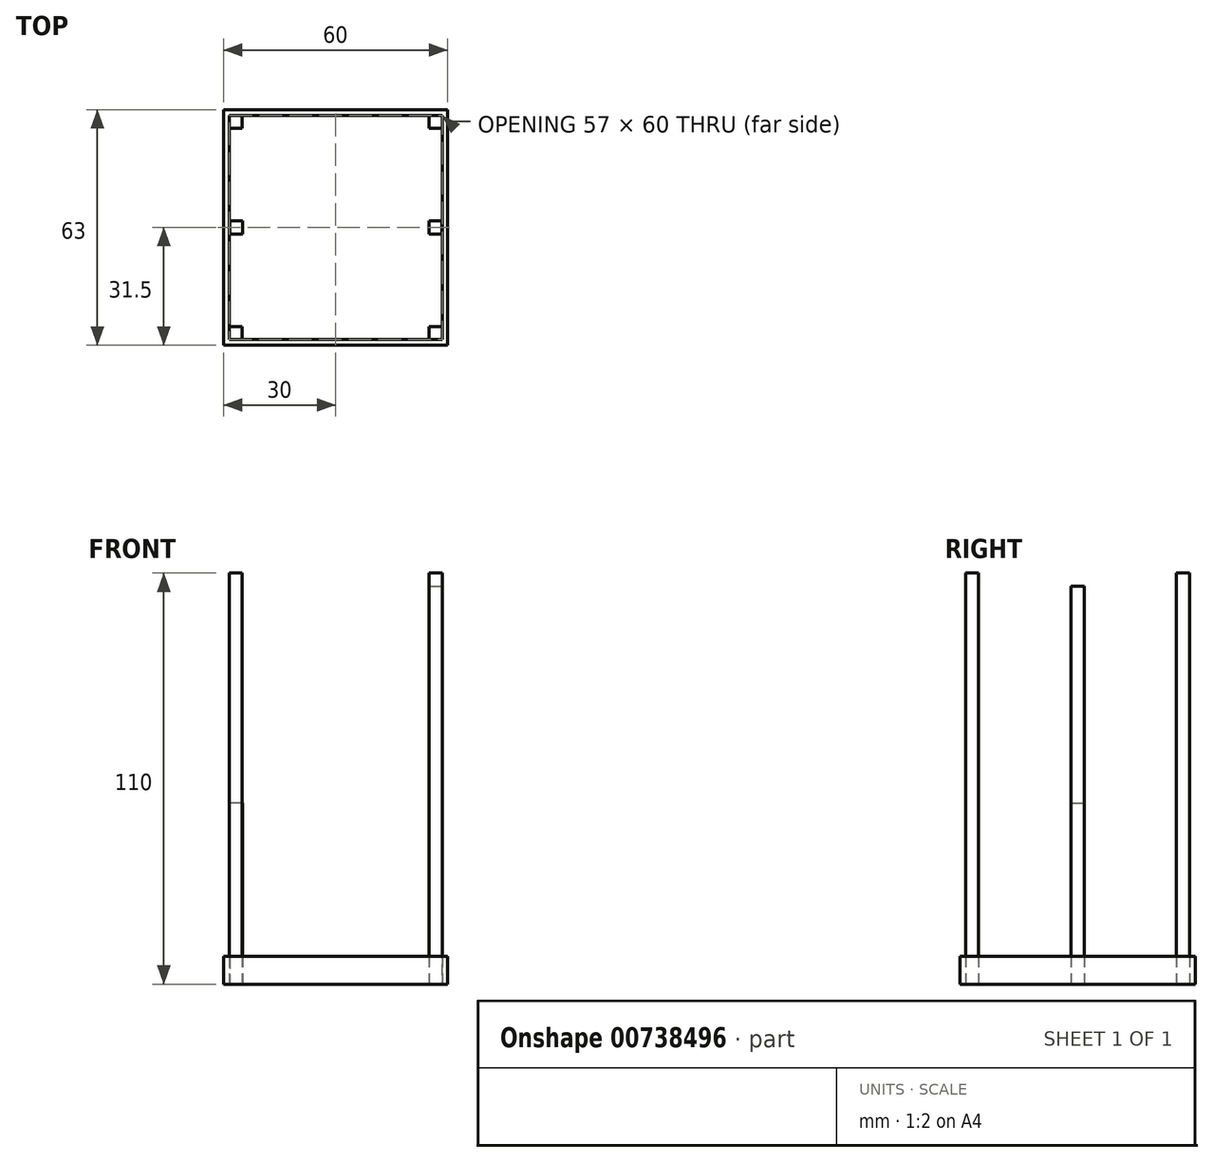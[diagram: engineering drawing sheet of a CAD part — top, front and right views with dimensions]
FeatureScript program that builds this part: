
annotation { "Feature Type Name" : "Feature", "Feature Type Description" : "" }
export const myFeature = defineFeature(function(context is Context, id is Id, definition is map)
    precondition{}
    {
        {
            var Q0;
            Q0=qCreatedBy(makeId("Top.planeOp"),FACE);
            var sketch = newSketch(context, id + "F0", { "sketchPlane" : qUnion([Q0])});
            skLineSegment(sketch, "E0.bottom", {"start": v(30, -31.5) * mm, "end": v(-30, -31.5) * mm});
            skLineSegment(sketch, "E0.top", {"start": v(30, 31.5) * mm, "end": v(-30, 31.5) * mm});
            skLineSegment(sketch, "E0.left", {"start": v(30, -31.5) * mm, "end": v(30, 31.5) * mm});
            skLineSegment(sketch, "E0.right", {"start": v(-30, -31.5) * mm, "end": v(-30, 31.5) * mm});
            skPoint(sketch, "E0.middle", {"position": v(0, 0) * mm});
            skLineSegment(sketch, "E1", {"start": v(30, 30) * mm, "end": v(-30, 30) * mm});
            skLineSegment(sketch, "E2", {"start": v(-28.5, 30) * mm, "end": v(-28.5, -30) * mm});
            skLineSegment(sketch, "E3", {"start": v(28.5, 30) * mm, "end": v(28.5, -30) * mm});
            skLineSegment(sketch, "E4.bottom", {"start": v(-28.5, -30) * mm, "end": v(-25, -30) * mm});
            skLineSegment(sketch, "E4.top", {"start": v(-28.5, -26.5) * mm, "end": v(-25, -26.5) * mm});
            skLineSegment(sketch, "E4.left", {"start": v(-28.5, -30) * mm, "end": v(-28.5, -26.5) * mm});
            skLineSegment(sketch, "E4.right", {"start": v(-25, -30) * mm, "end": v(-25, -26.5) * mm});
            skLineSegment(sketch, "E5.bottom", {"start": v(-28.5, 30) * mm, "end": v(-25, 30) * mm});
            skLineSegment(sketch, "E5.top", {"start": v(-28.5, 26.5) * mm, "end": v(-25, 26.5) * mm});
            skLineSegment(sketch, "E5.left", {"start": v(-28.5, 30) * mm, "end": v(-28.5, 26.5) * mm});
            skLineSegment(sketch, "E5.right", {"start": v(-25, 30) * mm, "end": v(-25, 26.5) * mm});
            skLineSegment(sketch, "E6.bottom", {"start": v(28.5, 30) * mm, "end": v(25, 30) * mm});
            skLineSegment(sketch, "E6.top", {"start": v(28.5, 26.5) * mm, "end": v(25, 26.5) * mm});
            skLineSegment(sketch, "E6.left", {"start": v(28.5, 30) * mm, "end": v(28.5, 26.5) * mm});
            skLineSegment(sketch, "E6.right", {"start": v(25, 30) * mm, "end": v(25, 26.5) * mm});
            skLineSegment(sketch, "E7.bottom", {"start": v(28.5, -30) * mm, "end": v(25, -30) * mm});
            skLineSegment(sketch, "E7.top", {"start": v(28.5, -26.5) * mm, "end": v(25, -26.5) * mm});
            skLineSegment(sketch, "E7.left", {"start": v(28.5, -30) * mm, "end": v(28.5, -26.5) * mm});
            skLineSegment(sketch, "E7.right", {"start": v(25, -30) * mm, "end": v(25, -26.5) * mm});
            skLineSegment(sketch, "E8.bottom", {"start": v(24.95, -1.75) * mm, "end": v(28.45, -1.75) * mm});
            skLineSegment(sketch, "E8.top", {"start": v(24.95, 1.75) * mm, "end": v(28.45, 1.75) * mm});
            skLineSegment(sketch, "E8.left", {"start": v(24.95, -1.75) * mm, "end": v(24.95, 1.75) * mm});
            skLineSegment(sketch, "E8.right", {"start": v(28.45, -1.75) * mm, "end": v(28.45, 1.75) * mm});
            skPoint(sketch, "E8.middle", {"position": v(26.7, 0) * mm});
            skPoint(sketch, "E8.middle.positionSnap0", {"position": v(28.5, 0) * mm});
            skPoint(sketch, "E8.centerSnap0", {"position": v(28.5, 0) * mm});
            skLineSegment(sketch, "E9.bottom", {"start": v(-24.87, -1.75) * mm, "end": v(-28.37, -1.75) * mm});
            skLineSegment(sketch, "E9.top", {"start": v(-24.87, 1.75) * mm, "end": v(-28.37, 1.75) * mm});
            skLineSegment(sketch, "E9.left", {"start": v(-24.87, -1.75) * mm, "end": v(-24.87, 1.75) * mm});
            skLineSegment(sketch, "E9.right", {"start": v(-28.37, -1.75) * mm, "end": v(-28.37, 1.75) * mm});
            skPoint(sketch, "E9.middle", {"position": v(-26.62, 0) * mm});
            skPoint(sketch, "E9.middle.positionSnap0", {"position": v(-28.5, 0) * mm});
            skPoint(sketch, "E9.centerSnap0", {"position": v(-28.5, 0) * mm});
            skLineSegment(sketch, "E10", {"start": v(-30, -30) * mm, "end": v(30, -30) * mm});
            skSolve(sketch);
        }
        {
            var Q0;
            {var subQ3=sQuery(id+"F0.wireOp",EDGE,"E10");var subQ4=sQuery(id+"F0.wireOp",EDGE,"E0.left");var subQ5=makeQuery(id+"F0.imprint","INTERSECT",VERTEX,{"derivedFrom":[subQ4,subQ3]});Q0=makeQuery(id+"F0.imprint","IMPRINT",FACE,{"disambiguationData":[TD([[makeQuery(id+"F0.imprint","IMPRINT",EDGE,{"disambiguationData":[TD([[subQ5,-1.0]])],"derivedFrom":subQ4}),1.0]])]});}
            extrude(context, id + "F1", {"entities" : qUnion([Q0]), "depth" : 7.5 * mm, "offsetDistance" : 25 * mm});
        }
        {
            var Q0;
            {var subQ4=sQuery(id+"F0.wireOp",EDGE,"E0.top");Q0=makeQuery(id+"F0.imprint","IMPRINT",FACE,{"disambiguationData":[TD([[makeQuery(id+"F0.imprint","IMPRINT",EDGE,{"derivedFrom":subQ4}),1.0]])]});}
            extrude(context, id + "F2", {"entities" : qUnion([Q0]), "operationType" : NewBodyOperationType.ADD, "depth" : 7.5 * mm, "offsetDistance" : 25 * mm});
        }
        {
            var Q0;
            {var subQ1=sQuery(id+"F0.wireOp",EDGE,"E0.bottom");Q0=makeQuery(id+"F0.imprint","IMPRINT",FACE,{"disambiguationData":[TD([[makeQuery(id+"F0.imprint","IMPRINT",EDGE,{"derivedFrom":subQ1}),-1.0]])]});}
            var Q1;
            {var subQ0=sQuery(id+"F0.wireOp",EDGE,"E10");var subQ6=sQuery(id+"F0.wireOp",EDGE,"E0.right");var subQ9=makeQuery(id+"F0.imprint","INTERSECT",VERTEX,{"derivedFrom":[subQ6,subQ0]});Q1=makeQuery(id+"F0.imprint","IMPRINT",FACE,{"disambiguationData":[TD([[makeQuery(id+"F0.imprint","IMPRINT",EDGE,{"disambiguationData":[TD([[subQ9,-1.0]])],"derivedFrom":subQ6}),-1.0]])]});}
            extrude(context, id + "F3", {"entities" : qUnion([Q0, Q1]), "operationType" : NewBodyOperationType.ADD, "depth" : 7.5 * mm, "offsetDistance" : 25 * mm});
        }
        {
            var Q0;
            {var subQ4=sQuery(id+"F0.wireOp",EDGE,"E5.top");Q0=makeQuery(id+"F0.imprint","IMPRINT",FACE,{"disambiguationData":[TD([[makeQuery(id+"F0.imprint","IMPRINT",EDGE,{"derivedFrom":subQ4}),1.0]])]});}
            extrude(context, id + "F4", {"entities" : qUnion([Q0]), "operationType" : NewBodyOperationType.ADD, "depth" : 110 * mm, "offsetDistance" : 25 * mm});
        }
        {
            var Q0;
            {var subQ0=sQuery(id+"F0.wireOp",EDGE,"E4.bottom");Q0=makeQuery(id+"F0.imprint","IMPRINT",FACE,{"disambiguationData":[TD([[makeQuery(id+"F0.imprint","IMPRINT",EDGE,{"derivedFrom":subQ0}),1.0]])]});}
            var Q1;
            {var subQ0=sQuery(id+"F0.wireOp",EDGE,"E7.bottom");Q1=makeQuery(id+"F0.imprint","IMPRINT",FACE,{"disambiguationData":[TD([[makeQuery(id+"F0.imprint","IMPRINT",EDGE,{"derivedFrom":subQ0}),-1.0]])]});}
            var Q2;
            {var subQ4=sQuery(id+"F0.wireOp",EDGE,"E6.top");Q2=makeQuery(id+"F0.imprint","IMPRINT",FACE,{"disambiguationData":[TD([[makeQuery(id+"F0.imprint","IMPRINT",EDGE,{"derivedFrom":subQ4}),-1.0]])]});}
            extrude(context, id + "F5", {"entities" : qUnion([Q0, Q1, Q2]), "operationType" : NewBodyOperationType.ADD, "depth" : 110 * mm, "offsetDistance" : 25 * mm});
        }
        {
            var Q0;
            Q0=makeQuery(id+"F0.imprint","IMPRINT",FACE,{"disambiguationData":[TD([[makeQuery(id+"F0.imprint","IMPRINT",EDGE,{"derivedFrom":sQuery(id+"F0.wireOp",EDGE,"E9.bottom")}),-1.0]])]});
            extrude(context, id + "F6", {"entities" : qUnion([Q0]), "depth" : 48.5 * mm, "offsetDistance" : 25 * mm});
        }
        {
            var Q0;
            Q0=makeQuery(id+"F0.imprint","IMPRINT",FACE,{"disambiguationData":[TD([[makeQuery(id+"F0.imprint","IMPRINT",EDGE,{"derivedFrom":sQuery(id+"F0.wireOp",EDGE,"E8.bottom")}),1.0]])]});
            extrude(context, id + "F7", {"entities" : qUnion([Q0]), "depth" : 106.5 * mm, "offsetDistance" : 25 * mm});
        }
        {
            var Q0;
            Q0=qCreatedBy(makeId("Top.planeOp"),FACE);
            cPlane(context, id + "F8", {"entities" : qUnion([Q0]), "cplaneType" : CPlaneType.OFFSET, "offset" : 37 * mm, "width" : 150 * mm, "height" : 150 * mm});
        }
    });
